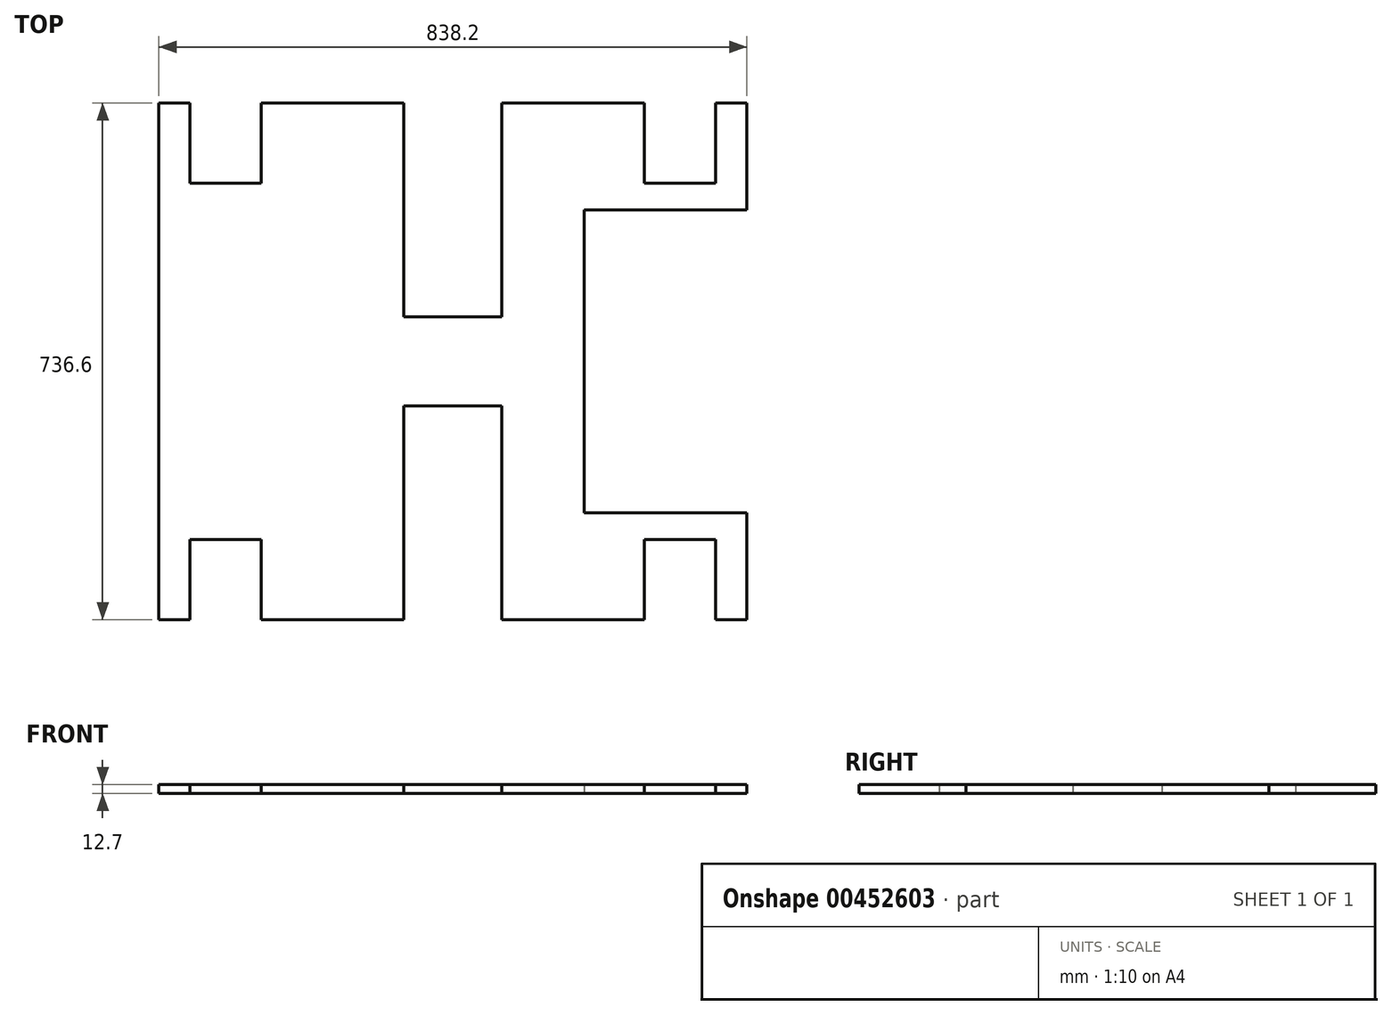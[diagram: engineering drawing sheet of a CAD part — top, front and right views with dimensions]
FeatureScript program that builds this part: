
annotation { "Feature Type Name" : "Feature", "Feature Type Description" : "" }
export const myFeature = defineFeature(function(context is Context, id is Id, definition is map)
    precondition{}
    {
        {
            var Q0;
            Q0=qCreatedBy(makeId("Top.planeOp"),FACE);
            var sketch = newSketch(context, id + "F0", { "sketchPlane" : qUnion([Q0])});
            skLineSegment(sketch, "E0.bottom", {"start": v(187.32, 160.02) * mm, "end": v(419.1, 160.02) * mm});
            skLineSegment(sketch, "E0.top", {"start": v(187.33, -271.78) * mm, "end": v(419.1, -271.78) * mm});
            skLineSegment(sketch, "E0.left", {"start": v(187.32, 160.02) * mm, "end": v(187.33, -271.78) * mm});
            skLineSegment(sketch, "E1.bottom", {"start": v(69.85, -119.38) * mm, "end": v(-69.85, -119.38) * mm});
            skPoint(sketch, "E1.middle", {"position": v(0, -249.8) * mm});
            skLineSegment(sketch, "E2", {"start": v(187.32, -55.88) * mm, "end": v(-164.93, -55.88) * mm, "construction": true});
            skLineSegment(sketch, "E3.MirrorCS", {"start": v(69.85, 7.62) * mm, "end": v(-69.85, 7.62) * mm});
            skLineSegment(sketch, "E4.bottom", {"start": v(273.05, 198.12) * mm, "end": v(374.65, 198.12) * mm});
            skLineSegment(sketch, "E5.MirrorCS", {"start": v(273.05, -309.88) * mm, "end": v(374.65, -309.88) * mm});
            skLineSegment(sketch, "E6", {"start": v(0, -249.8) * mm, "end": v(0, 491.19) * mm, "construction": true});
            skLineSegment(sketch, "E7.MirrorCS", {"start": v(-273.05, 198.12) * mm, "end": v(-374.65, 198.12) * mm});
            skLineSegment(sketch, "E8.MirrorCS", {"start": v(-273.05, -309.88) * mm, "end": v(-374.65, -309.88) * mm});
            skLineSegment(sketch, "E9", {"start": v(-419.1, 312.42) * mm, "end": v(-374.65, 312.42) * mm});
            skLineSegment(sketch, "E10", {"start": v(-419.1, -424.18) * mm, "end": v(-374.65, -424.18) * mm});
            skLineSegment(sketch, "E11.trimOffspring", {"start": v(-273.05, -424.18) * mm, "end": v(-69.85, -424.18) * mm});
            skLineSegment(sketch, "E12.trimOffspring", {"start": v(374.65, -424.18) * mm, "end": v(419.1, -424.18) * mm});
            skLineSegment(sketch, "E13.trimOffspring", {"start": v(-273.05, 312.42) * mm, "end": v(-69.85, 312.42) * mm});
            skLineSegment(sketch, "E14.trimOffspring", {"start": v(374.65, 312.42) * mm, "end": v(419.1, 312.42) * mm});
            skLineSegment(sketch, "E15.trimOffspring", {"start": v(69.85, 312.42) * mm, "end": v(273.05, 312.42) * mm});
            skLineSegment(sketch, "E16.trimOffspring", {"start": v(69.85, -424.18) * mm, "end": v(273.05, -424.18) * mm});
            skLineSegment(sketch, "E17", {"start": v(69.85, -424.18) * mm, "end": v(69.85, -119.38) * mm});
            skLineSegment(sketch, "E18", {"start": v(-69.85, -119.38) * mm, "end": v(-69.85, -424.18) * mm});
            skLineSegment(sketch, "E19", {"start": v(-374.65, -309.88) * mm, "end": v(-374.65, -424.18) * mm});
            skLineSegment(sketch, "E20", {"start": v(-273.05, -424.18) * mm, "end": v(-273.05, -309.88) * mm});
            skLineSegment(sketch, "E21", {"start": v(273.05, -309.88) * mm, "end": v(273.05, -424.18) * mm});
            skLineSegment(sketch, "E22", {"start": v(374.65, -309.88) * mm, "end": v(374.65, -424.18) * mm});
            skLineSegment(sketch, "E23", {"start": v(-374.65, 312.42) * mm, "end": v(-374.65, 198.12) * mm});
            skLineSegment(sketch, "E24", {"start": v(-273.05, 312.42) * mm, "end": v(-273.05, 198.12) * mm});
            skLineSegment(sketch, "E25", {"start": v(-69.85, 312.42) * mm, "end": v(-69.85, 7.62) * mm});
            skLineSegment(sketch, "E26", {"start": v(69.85, 312.42) * mm, "end": v(69.85, 7.62) * mm});
            skLineSegment(sketch, "E27", {"start": v(273.05, 312.42) * mm, "end": v(273.05, 198.12) * mm});
            skLineSegment(sketch, "E28", {"start": v(374.65, 312.42) * mm, "end": v(374.65, 198.12) * mm});
            skLineSegment(sketch, "E29", {"start": v(-419.1, 312.42) * mm, "end": v(-419.1, -424.18) * mm});
            skLineSegment(sketch, "E30", {"start": v(419.1, -424.18) * mm, "end": v(419.1, -271.78) * mm});
            skLineSegment(sketch, "E31", {"start": v(419.1, 312.42) * mm, "end": v(419.1, 160.02) * mm});
            skSolve(sketch);
        }
        {
            var Q0;
            Q0=makeQuery(id+"F0.imprint","IMPRINT",FACE,{"disambiguationData":[TD([[makeQuery(id+"F0.imprint","IMPRINT",EDGE,{"derivedFrom":sQuery(id+"F0.wireOp",EDGE,"E0.bottom")}),1.0]])]});
            extrude(context, id + "F1", {"entities" : qUnion([Q0]), "depth" : 12.7 * mm});
        }
    });
